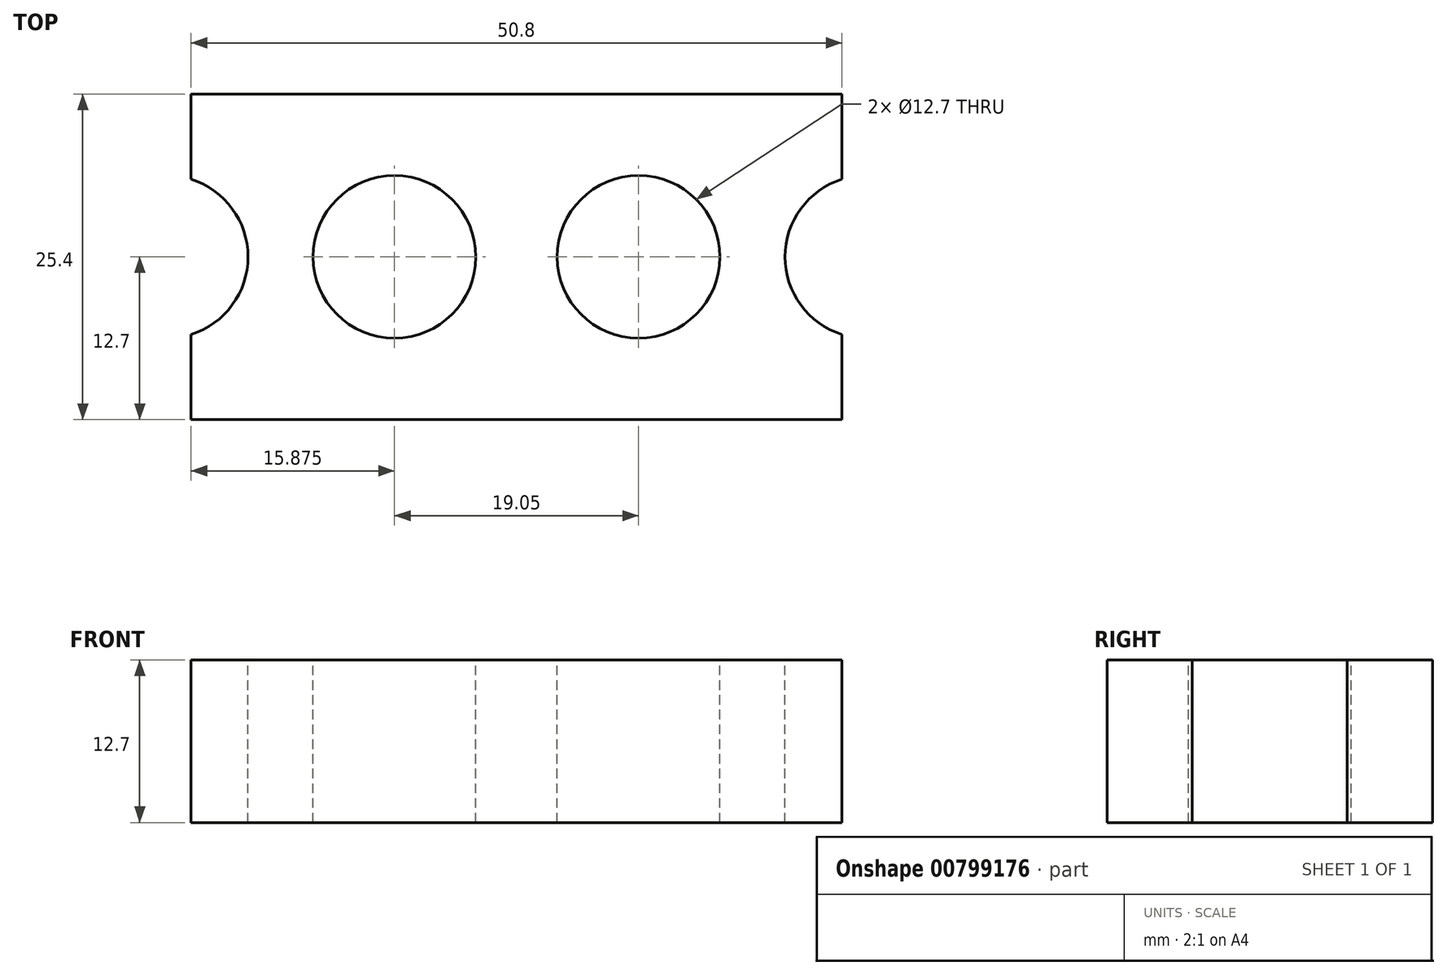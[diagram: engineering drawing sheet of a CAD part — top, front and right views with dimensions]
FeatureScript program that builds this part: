
annotation { "Feature Type Name" : "Feature", "Feature Type Description" : "" }
export const myFeature = defineFeature(function(context is Context, id is Id, definition is map)
    precondition{}
    {
        {
            var Q0;
            Q0=qCreatedBy(makeId("Top.planeOp"),FACE);
            var sketch = newSketch(context, id + "F0", { "sketchPlane" : qUnion([Q0])});
            skLineSegment(sketch, "E0.bottom", {"start": v(-25.4, 12.7) * mm, "end": v(25.4, 12.7) * mm});
            skLineSegment(sketch, "E0.top", {"start": v(-25.4, -12.7) * mm, "end": v(25.4, -12.7) * mm});
            skLineSegment(sketch, "E0.left", {"start": v(-25.4, 12.7) * mm, "end": v(-25.4, -12.7) * mm});
            skLineSegment(sketch, "E0.right", {"start": v(25.4, 12.7) * mm, "end": v(25.4, -12.7) * mm});
            skLineSegment(sketch, "E1", {"start": v(-25.4, -12.7) * mm, "end": v(25.4, 12.7) * mm, "construction": true});
            skSolve(sketch);
        }
        {
            var Q0;
            Q0=qSketchRegion(id+"F0",true);
            extrude(context, id + "F1", {"entities" : qUnion([Q0]), "endBound" : BoundingType.SYMMETRIC, "depth" : 12.7 * mm});
        }
        {
            var Q0;
            Q0=makeQuery(id+"F1.opExtrude","CAP_FACE",FACE,{"disambiguationData":[OSD([sQuery(id+"F0.wireOp",EDGE,"E0.bottom"),sQuery(id+"F0.wireOp",EDGE,"E0.top"),sQuery(id+"F0.wireOp",EDGE,"E0.left"),sQuery(id+"F0.wireOp",EDGE,"E0.right")])],"isStart":false});
            var sketch = newSketch(context, id + "F2", { "sketchPlane" : qUnion([Q0])});
            skCircle(sketch, "E2", {"center": v(-27.3, 0) * mm, "radius": 6.35 * mm});
            skCircle(sketch, "E3", {"center": v(-9.53, 0) * mm, "radius": 6.35 * mm});
            skCircle(sketch, "E4", {"center": v(27.3, 0) * mm, "radius": 6.35 * mm});
            skCircle(sketch, "E5", {"center": v(9.53, 0) * mm, "radius": 6.35 * mm});
            skLineSegment(sketch, "E6", {"start": v(-9.53, 0) * mm, "end": v(9.53, 0) * mm, "construction": true});
            skSolve(sketch);
        }
        {
            var Q0;
            Q0=qSketchRegion(id+"F2",true);
            extrude(context, id + "F3", {"entities" : qUnion([Q0]), "operationType" : NewBodyOperationType.REMOVE, "endBound" : BoundingType.THROUGH_ALL, "oppositeDirection" : true, "depth" : 25.4 * mm});
        }
    });
